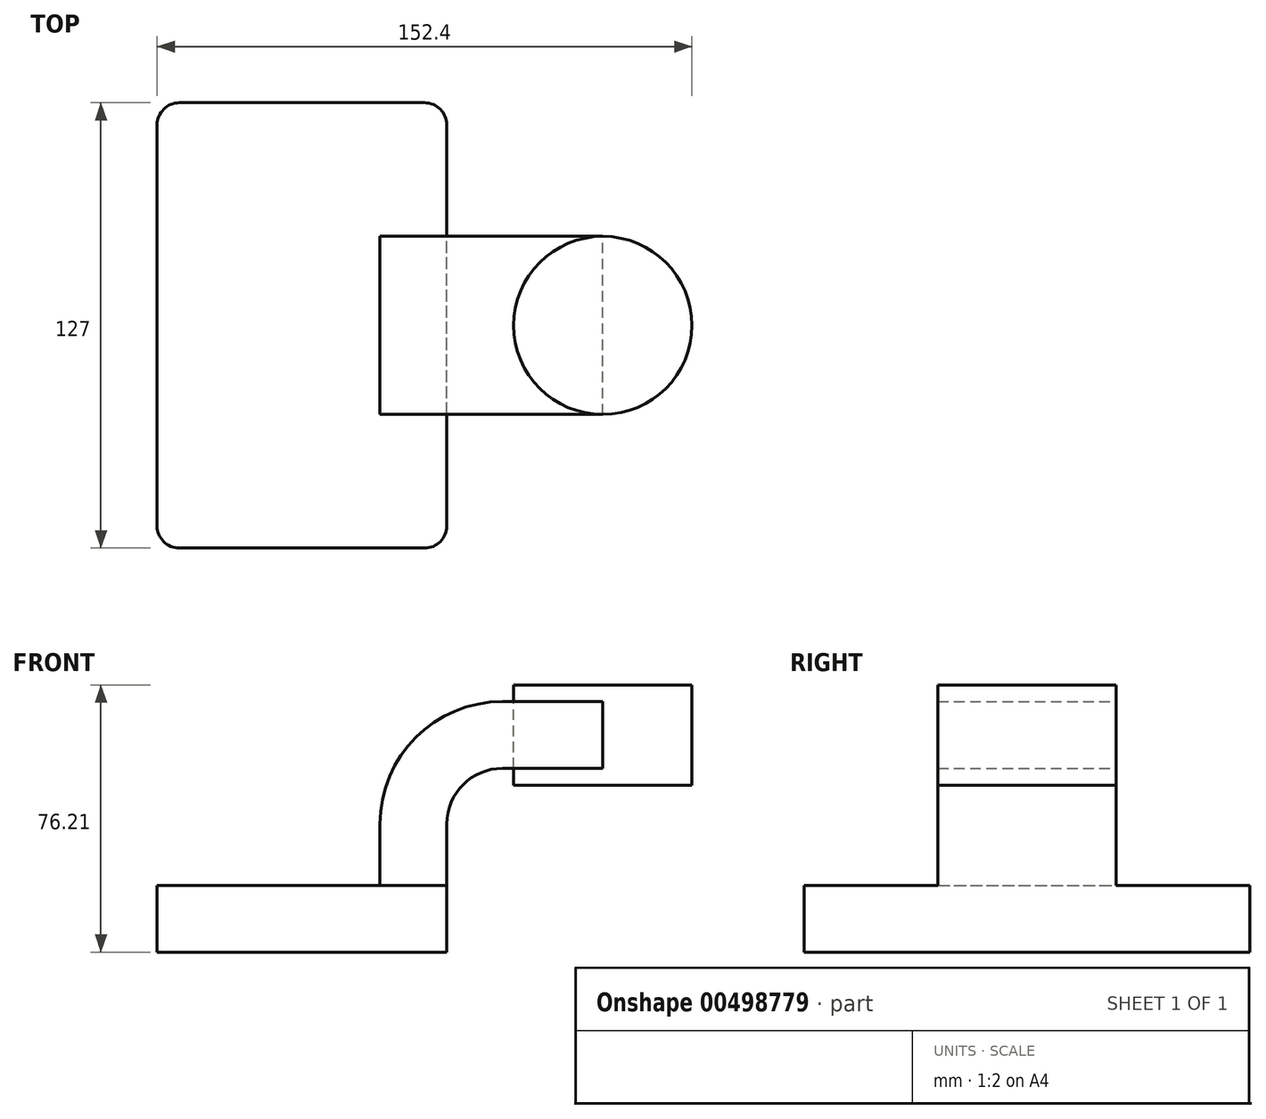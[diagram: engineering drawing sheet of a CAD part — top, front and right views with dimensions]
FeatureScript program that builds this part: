
annotation { "Feature Type Name" : "Feature", "Feature Type Description" : "" }
export const myFeature = defineFeature(function(context is Context, id is Id, definition is map)
    precondition{}
    {
        {
            var Q0;
            Q0=qCreatedBy(makeId("Front.planeOp"),FACE);
            var sketch = newSketch(context, id + "F0", { "sketchPlane" : qUnion([Q0])});
            skLineSegment(sketch, "E0.bottom", {"start": v(-41.28, 9.52) * mm, "end": v(41.28, 9.53) * mm});
            skLineSegment(sketch, "E0.top", {"start": v(-41.27, -9.52) * mm, "end": v(41.28, -9.52) * mm});
            skLineSegment(sketch, "E0.left", {"start": v(-41.28, 9.52) * mm, "end": v(-41.28, -9.53) * mm});
            skLineSegment(sketch, "E0.right", {"start": v(41.27, 9.53) * mm, "end": v(41.28, -9.52) * mm});
            skPoint(sketch, "E0.middle", {"position": v(0, 0) * mm});
            skLineSegment(sketch, "E1.bottom", {"start": v(111.12, 66.68) * mm, "end": v(60.32, 66.68) * mm});
            skLineSegment(sketch, "E1.top", {"start": v(111.12, 38.1) * mm, "end": v(60.32, 38.1) * mm});
            skLineSegment(sketch, "E1.left", {"start": v(111.12, 66.67) * mm, "end": v(111.12, 38.1) * mm});
            skLineSegment(sketch, "E1.right", {"start": v(60.32, 66.68) * mm, "end": v(60.32, 38.1) * mm});
            skPoint(sketch, "E1.middle", {"position": v(85.72, 52.39) * mm});
            skLineSegment(sketch, "E2", {"start": v(41.27, 9.53) * mm, "end": v(41.27, 27) * mm});
            skArc(sketch, "E3", {"start": v(41.27, 27) * mm, "mid": v(45.92, 38.23) * mm, "end": v(57.15, 42.88) * mm});
            skLineSegment(sketch, "E4", {"start": v(57.15, 42.88) * mm, "end": v(85.73, 42.88) * mm});
            skLineSegment(sketch, "E5.0", {"start": v(57.15, 61.93) * mm, "end": v(85.72, 61.93) * mm});
            skArc(sketch, "E5.1", {"start": v(22.22, 27) * mm, "mid": v(32.45, 51.7) * mm, "end": v(57.15, 61.93) * mm});
            skLineSegment(sketch, "E5.2", {"start": v(22.22, 9.53) * mm, "end": v(22.22, 27) * mm});
            skFitSpline(sketch, "E6", {"points": [v(-41.28, 9.53) * mm, v(57.15, 61.93) * mm], "startDerivative": vector(68.41, 127.23) * mm, "endDerivative": vector(97.58, -2.35) * mm});
            skLineSegment(sketch, "E7", {"start": v(85.73, 61.93) * mm, "end": v(85.73, 42.88) * mm});
            skPoint(sketch, "E8", {"position": v(85.72, 66.68) * mm});
            skLineSegment(sketch, "E9", {"start": v(85.72, 61.93) * mm, "end": v(85.72, 66.68) * mm});
            skLineSegment(sketch, "E10", {"start": v(85.72, 42.88) * mm, "end": v(85.72, 38.1) * mm});
            skSolve(sketch);
        }
        {
            var Q0;
            Q0=makeQuery(id+"F0.imprint","IMPRINT",FACE,{"disambiguationData":[TD([[makeQuery(id+"F0.imprint","IMPRINT",EDGE,{"derivedFrom":sQuery(id+"F0.wireOp",EDGE,"E0.top")}),1.0]])]});
            extrude(context, id + "F1", {"entities" : qUnion([Q0]), "endBound" : BoundingType.SYMMETRIC, "depth" : 127 * mm});
        }
        {
            var Q0;
            {var subQ1=sQuery(id+"F0.wireOp",EDGE,"E2");Q0=makeQuery(id+"F0.imprint","IMPRINT",FACE,{"disambiguationData":[TD([[makeQuery(id+"F0.imprint","IMPRINT",EDGE,{"derivedFrom":subQ1}),1.0]])]});}
            var Q1;
            {var subQ5=sQuery(id+"F0.wireOp",EDGE,"E7");Q1=makeQuery(id+"F0.imprint","IMPRINT",FACE,{"disambiguationData":[TD([[makeQuery(id+"F0.imprint","IMPRINT",EDGE,{"derivedFrom":subQ5}),-1.0]])]});}
            extrude(context, id + "F2", {"entities" : qUnion([Q0, Q1]), "operationType" : NewBodyOperationType.ADD, "endBound" : BoundingType.SYMMETRIC, "depth" : 50.8 * mm});
        }
        {
            var Q0;
            Q0=makeQuery(id+"F0.imprint","IMPRINT",FACE,{"disambiguationData":[TD([[makeQuery(id+"F0.imprint","IMPRINT",EDGE,{"derivedFrom":sQuery(id+"F0.wireOp",EDGE,"E5.1")}),1.0]])]});
            extrude(context, id + "F3", {"entities" : qUnion([Q0]), "operationType" : NewBodyOperationType.ADD, "endBound" : BoundingType.SYMMETRIC, "depth" : 15.88 * mm});
        }
        {
            var Q0;
            {var subQ0=sQuery(id+"F0.wireOp",EDGE,"E1.left");Q0=makeQuery(id+"F0.imprint","IMPRINT",FACE,{"disambiguationData":[TD([[makeQuery(id+"F0.imprint","IMPRINT",EDGE,{"derivedFrom":subQ0}),-1.0]])]});}
            var Q1;
            Q1=sQuery(id+"F0.wireOp",EDGE,"E7");
            revolve(context, id + "F4", {"entities" : qUnion([Q0]), "axis" : qUnion([Q1]), "revolveType" : RevolveType.FULL});
        }
        {
            var Q0;
            Q0=makeQuery(id+"F1.opExtrude","CAP_EDGE",EDGE,{"disambiguationData":[OSD([sQuery(id+"F0.wireOp",EDGE,"E0.right")])],"isStart":false});
            var Q1;
            Q1=makeQuery(id+"F1.opExtrude","CAP_EDGE",EDGE,{"disambiguationData":[OSD([sQuery(id+"F0.wireOp",EDGE,"E0.right")])],"isStart":true});
            var Q2;
            Q2=makeQuery(id+"F1.opExtrude","CAP_EDGE",EDGE,{"disambiguationData":[OSD([sQuery(id+"F0.wireOp",EDGE,"E0.left")])],"isStart":true});
            var Q3;
            Q3=makeQuery(id+"F1.opExtrude","CAP_EDGE",EDGE,{"disambiguationData":[OSD([sQuery(id+"F0.wireOp",EDGE,"E0.left")])],"isStart":false});
            fillet(context, id + "F5", {"entities" : qUnion([Q0, Q1, Q2, Q3]), "radius" : 6.35 * mm, "tangentPropagation" : true, "allowEdgeOverflow" : false});
        }
    });
